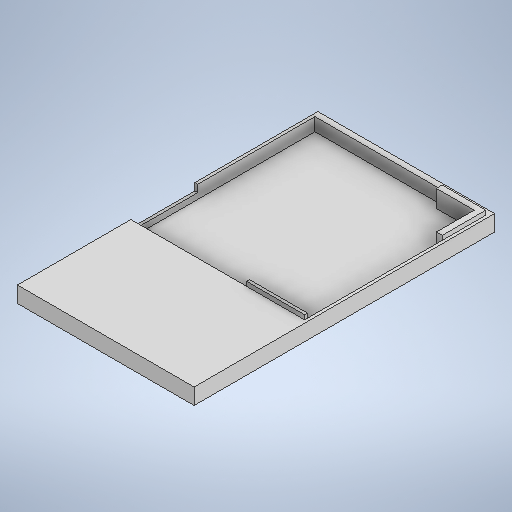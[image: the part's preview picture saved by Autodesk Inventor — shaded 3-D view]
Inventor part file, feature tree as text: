
AUTODESK INVENTOR PART (.ipt)
format: ipt  version: 2025.2 (Build 292293000, 293)  size: 293,888 bytes
history: native  units: mm
features: extrude x5, sketch x5
ambient origin geometry x8: Origin, YZ Plane, XZ Plane, XY Plane, X Axis, Y Axis, Z Axis, Center Point
bodies: Solid1 (feature_tree)
feature tree (10):
  extrude  "Extrusion1"  Depth=103.298mm
  extrude  "Extrusion2"  Depth=39.0mm
  extrude  "Extrusion3"  Depth=1.0mm
  extrude  "Extrusion4"  Depth=1.0mm
  extrude  "Extrusion5"  Depth=4.5mm TaperAngle=0.0deg
  sketch  "Sketch1"  dims[d0=60.74mm d1=103.298mm]
  sketch  "Sketch2"  dims[d2=1.0mm d3=0.0mm d4=39.0mm]
  sketch  "Sketch3"  dims[d5=4.5mm d6=0.0mm d7=1.0mm]
  sketch  "Sketch4"  dims[d8=2.0mm d9=1.0mm]
  sketch  "Sketch5"  dims[d10=0.0mm d11=4.5mm d12=0.0mm d13=22.0mm d14=2.0mm d15=0.0mm d16=2.0mm d17=15.0mm d18=2.0mm d19=15.0mm d20=1.0mm d21=20.0mm d22=6.0mm d23=0.0mm]
